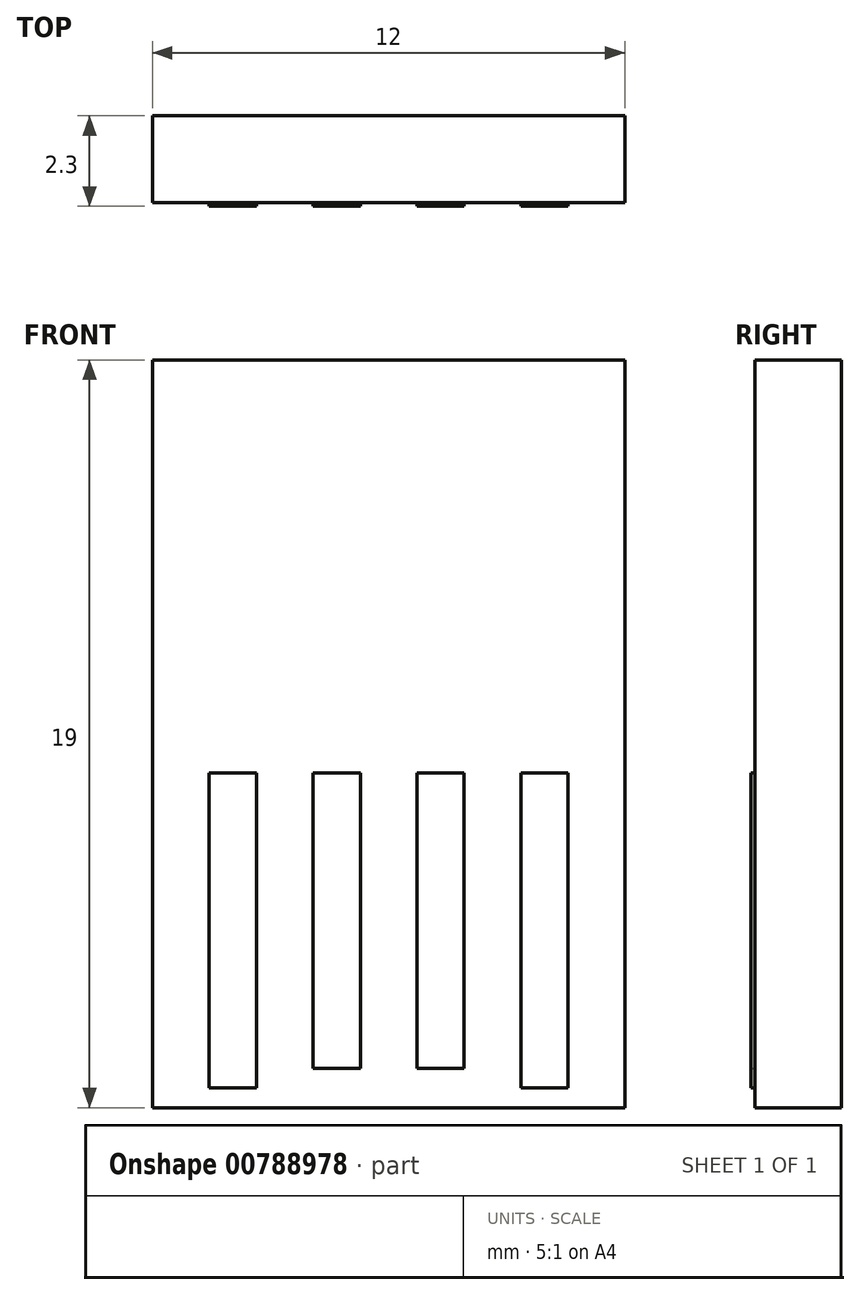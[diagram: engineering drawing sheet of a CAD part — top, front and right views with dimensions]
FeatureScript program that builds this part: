
annotation { "Feature Type Name" : "Feature", "Feature Type Description" : "" }
export const myFeature = defineFeature(function(context is Context, id is Id, definition is map)
    precondition{}
    {
        {
            var Q0;
            Q0=qCreatedBy(makeId("Top.planeOp"),FACE);
            var sketch = newSketch(context, id + "F0", { "sketchPlane" : qUnion([Q0])});
            skLineSegment(sketch, "E0.bottom", {"start": v(6, -1.1) * mm, "end": v(-6, -1.1) * mm});
            skLineSegment(sketch, "E0.top", {"start": v(6, 1.1) * mm, "end": v(-6, 1.1) * mm});
            skLineSegment(sketch, "E0.left", {"start": v(6, -1.1) * mm, "end": v(6, 1.1) * mm});
            skLineSegment(sketch, "E0.right", {"start": v(-6, -1.1) * mm, "end": v(-6, 1.1) * mm});
            skPoint(sketch, "E0.middle", {"position": v(0, 0) * mm});
            skSolve(sketch);
        }
        {
            var Q0;
            Q0 = qSketchRegion(id + "F0", true);
            extrude(context, id + "F1", {"entities" : qUnion([Q0]), "depth" : 19 * mm, "offsetDistance" : 25 * mm});
        }
        {
            var Q0;
            Q0=makeQuery(id+"F1.opExtrude","SWEPT_FACE",FACE,{"disambiguationData":[OSD([sQuery(id+"F0.wireOp",EDGE,"E0.bottom")])]});
            var sketch = newSketch(context, id + "F2", { "sketchPlane" : qUnion([Q0])});
            skLineSegment(sketch, "E1.bottom", {"start": v(-4.56, 0.5) * mm, "end": v(-3.36, 0.5) * mm});
            skLineSegment(sketch, "E1.top", {"start": v(-4.56, 8.5) * mm, "end": v(-3.36, 8.5) * mm});
            skLineSegment(sketch, "E1.left", {"start": v(-4.56, 0.5) * mm, "end": v(-4.56, 8.5) * mm});
            skLineSegment(sketch, "E1.right", {"start": v(-3.36, 0.5) * mm, "end": v(-3.36, 8.5) * mm});
            skLineSegment(sketch, "E2.bottom", {"start": v(4.56, 0.5) * mm, "end": v(3.36, 0.5) * mm});
            skLineSegment(sketch, "E2.top", {"start": v(4.56, 8.5) * mm, "end": v(3.36, 8.5) * mm});
            skLineSegment(sketch, "E2.left", {"start": v(4.56, 0.5) * mm, "end": v(4.56, 8.5) * mm});
            skLineSegment(sketch, "E2.right", {"start": v(3.36, 0.5) * mm, "end": v(3.36, 8.5) * mm});
            skLineSegment(sketch, "E3.bottom", {"start": v(1.92, 1) * mm, "end": v(0.72, 1) * mm});
            skLineSegment(sketch, "E3.top", {"start": v(1.92, 8.5) * mm, "end": v(0.72, 8.5) * mm});
            skLineSegment(sketch, "E3.left", {"start": v(1.92, 1) * mm, "end": v(1.92, 8.5) * mm});
            skLineSegment(sketch, "E3.right", {"start": v(0.72, 1) * mm, "end": v(0.72, 8.5) * mm});
            skLineSegment(sketch, "E4.bottom", {"start": v(-0.72, 1) * mm, "end": v(-1.92, 1) * mm});
            skLineSegment(sketch, "E4.top", {"start": v(-0.72, 8.5) * mm, "end": v(-1.92, 8.5) * mm});
            skLineSegment(sketch, "E4.left", {"start": v(-0.72, 1) * mm, "end": v(-0.72, 8.5) * mm});
            skLineSegment(sketch, "E4.right", {"start": v(-1.92, 1) * mm, "end": v(-1.92, 8.5) * mm});
            skLineSegment(sketch, "E5", {"start": v(-13.23, 1) * mm, "end": v(13.38, 1) * mm, "construction": true});
            skLineSegment(sketch, "E6", {"start": v(-12.34, 8.5) * mm, "end": v(11.3, 8.5) * mm, "construction": true});
            skLineSegment(sketch, "E7", {"start": v(-4.56, 4.5) * mm, "end": v(-6, 4.5) * mm, "construction": true});
            skLineSegment(sketch, "E8", {"start": v(-3.36, 4.5) * mm, "end": v(-1.92, 4.5) * mm, "construction": true});
            skLineSegment(sketch, "E9", {"start": v(-0.72, 4.5) * mm, "end": v(0.72, 4.5) * mm, "construction": true});
            skLineSegment(sketch, "E10", {"start": v(1.92, 4.5) * mm, "end": v(3.36, 4.5) * mm, "construction": true});
            skLineSegment(sketch, "E11", {"start": v(4.56, 4.5) * mm, "end": v(6, 4.5) * mm, "construction": true});
            skLineSegment(sketch, "E12", {"start": v(-11.04, 0.5) * mm, "end": v(10.78, 0.5) * mm, "construction": true});
            skSolve(sketch);
        }
        {
            var Q0;
            Q0 = qSketchRegion(id + "F2", true);
            extrude(context, id + "F3", {"entities" : qUnion([Q0]), "operationType" : NewBodyOperationType.ADD, "depth" : 0.1 * mm, "offsetDistance" : 25 * mm});
        }
    });
